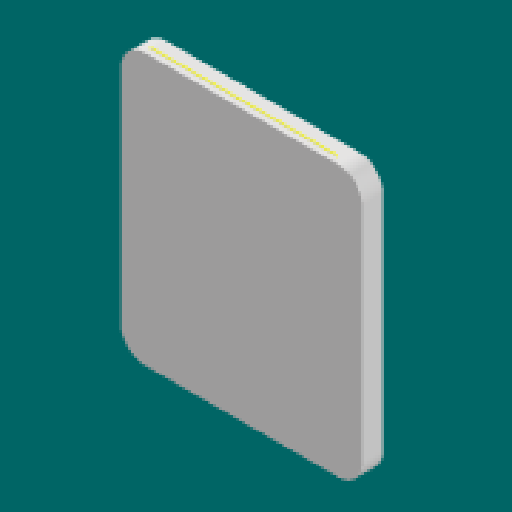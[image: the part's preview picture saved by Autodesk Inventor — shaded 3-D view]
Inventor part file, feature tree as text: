
AUTODESK INVENTOR PART (.ipt)
format: ipt  version: 2025.2 (Build 292293000, 293)  size: 272,896 bytes
history: native  units: mm
features: reference x29, extrude x6, sketch x6, other x4, plane x2, fillet x1
ambient origin geometry x8: Origin, YZ Plane, XZ Plane, XY Plane, X Axis, Y Axis, Z Axis, Center Point
bodies: Solid1 (feature_tree)
feature tree (48):
  plane  "Work Plane1"
  extrude  "Extrusion1"  Depth=2.0mm TaperAngle=0.0deg
  extrude  "Extrusion2"  Depth=7.0mm
  fillet  "Fillet1"  Radius=0.1mm
  sketch  "Sketch3"  dims[d7=0.1mm d8=0.1mm]
  plane  "Work Plane2"
  extrude  "Extrusion3"  Depth=0.1mm
  extrude  "Extrusion4"  Depth=1.0mm
  extrude  "Extrusion5"  Depth=3.0mm
  extrude  "Extrusion6"  Depth=1.0mm TaperAngle=0.0deg
  sketch  "Sketch1"  dims[d0=1.0mm d1=2.0mm d2=0.0mm]
  reference  "Reference1"
  reference  "Reference2"
  reference  "Reference3"
  reference  "Reference4"
  reference  "Reference5"
  reference  "Reference6"
  reference  "Reference7"
  reference  "Reference8"
  reference  "Reference9"
  reference  "Reference10"
  reference  "Reference11"
  reference  "Reference12"
  reference  "Reference13"
  reference  "Reference14"
  reference  "Reference15"
  reference  "Reference16"
  sketch  "Sketch2"  dims[d3=7.0mm d4=0.0mm d5=0.1mm d6=0.1mm]
  reference  "Reference17"
  reference  "Reference18"
  reference  "Reference19"
  reference  "Reference20"
  reference  "Reference21"
  sketch  "Sketch4"  dims[d9=1.0mm d10=1.5mm]
  sketch  "Sketch5"  dims[d11=3.88mm d12=0.0mm d13=3.0mm]
  sketch  "Sketch6"  dims[d14=10.0mm d15=0.0mm d16=1.0mm d17=0.0mm d18=20.0mm d19=20.0mm d20=5.65mm d21=0.0mm d22=0.5mm]
  reference  "Reference22"
  reference  "Reference23"
  reference  "Reference24"
  reference  "Reference25"
  reference  "Reference26"
  reference  "Reference27"
  reference  "Reference28"
  reference  "Reference29"
  other  "<userpath>\Downloads\cassing_hardware\Assembly1.iam"
  other  "Assembly1.iam"
  other  "AVR_MasImam:1"
  other  "ARDUINO-UNO_20:1"
